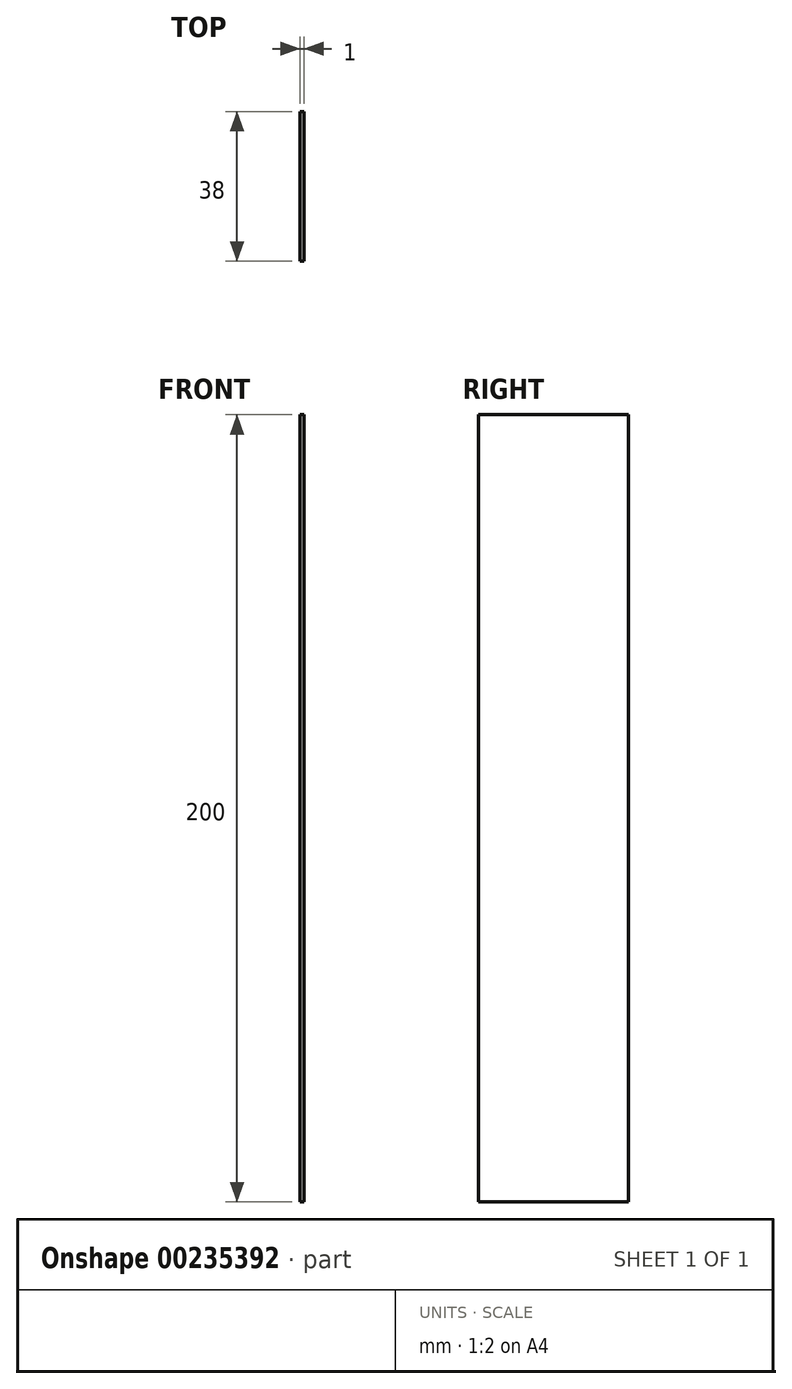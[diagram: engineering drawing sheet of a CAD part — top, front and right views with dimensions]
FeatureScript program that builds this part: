
annotation { "Feature Type Name" : "Feature", "Feature Type Description" : "" }
export const myFeature = defineFeature(function(context is Context, id is Id, definition is map)
    precondition{}
    {
        {
            var Q0;
            Q0=qCreatedBy(makeId("Right.planeOp"),FACE);
            var sketch = newSketch(context, id + "F0", { "sketchPlane" : qUnion([Q0])});
            skLineSegment(sketch, "E0.bottom", {"start": v(0, 0) * mm, "end": v(38, 0) * mm});
            skLineSegment(sketch, "E0.top", {"start": v(0, 200) * mm, "end": v(38, 200) * mm});
            skLineSegment(sketch, "E0.left", {"start": v(0, 0) * mm, "end": v(0, 200) * mm});
            skLineSegment(sketch, "E0.right", {"start": v(38, 0) * mm, "end": v(38, 200) * mm});
            skSolve(sketch);
        }
        {
            var Q0;
            Q0=makeQuery(id+"F0.imprint","IMPRINT",FACE,{"disambiguationData":[TD([[makeQuery(id+"F0.imprint","IMPRINT",EDGE,{"derivedFrom":sQuery(id+"F0.wireOp",EDGE,"E0.bottom")}),1.0]])]});
            extrude(context, id + "F1", {"entities" : qUnion([Q0]), "depth" : 1 * mm});
        }
    });
